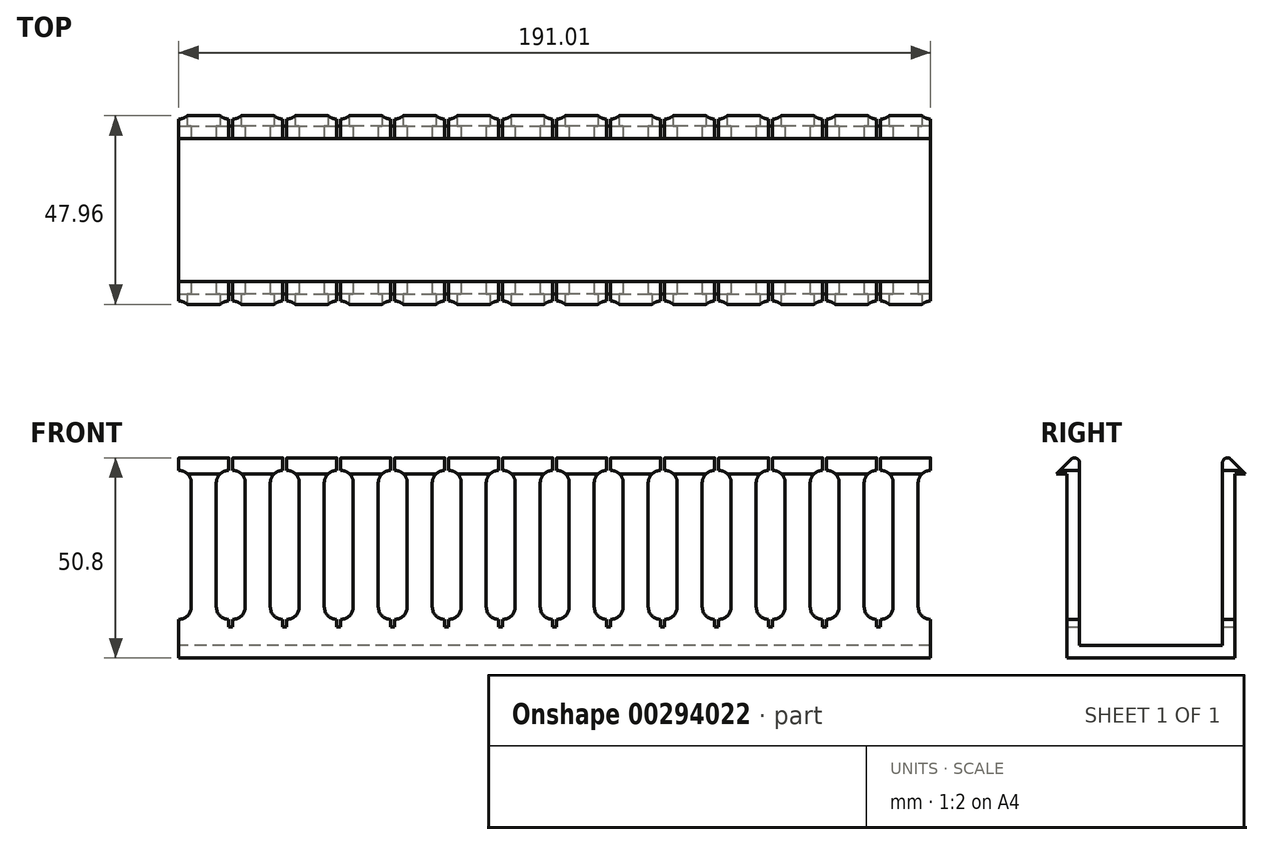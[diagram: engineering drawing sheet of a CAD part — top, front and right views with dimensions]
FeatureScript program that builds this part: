
annotation { "Feature Type Name" : "Feature", "Feature Type Description" : "" }
export const myFeature = defineFeature(function(context is Context, id is Id, definition is map)
    precondition{}
    {
        {
            var Q0;
            Q0=qCreatedBy(makeId("Right.planeOp"),FACE);
            var sketch = newSketch(context, id + "F0", { "sketchPlane" : qUnion([Q0])});
            skLineSegment(sketch, "E0", {"start": v(18.16, 7.87) * mm, "end": v(18.16, 49.53) * mm});
            skArc(sketch, "E1", {"start": v(20.33, 50.43) * mm, "mid": v(18.94, 50.7) * mm, "end": v(18.16, 49.53) * mm});
            skLineSegment(sketch, "E2", {"start": v(20.33, 50.43) * mm, "end": v(23.98, 46.78) * mm});
            skLineSegment(sketch, "E3", {"start": v(23.98, 46.78) * mm, "end": v(21.34, 46.78) * mm});
            skLineSegment(sketch, "E4", {"start": v(21.34, 46.78) * mm, "end": v(21.34, 7.87) * mm});
            skLineSegment(sketch, "E5", {"start": v(21.34, 7.87) * mm, "end": v(18.16, 7.87) * mm});
            skLineSegment(sketch, "E6", {"start": v(18.16, 7.87) * mm, "end": v(18.16, 3.18) * mm});
            skLineSegment(sketch, "E7", {"start": v(18.16, 3.18) * mm, "end": v(0, 3.17) * mm});
            skLineSegment(sketch, "E8", {"start": v(21.34, 7.87) * mm, "end": v(21.34, 0) * mm});
            skLineSegment(sketch, "E9", {"start": v(21.34, 0) * mm, "end": v(0, 0) * mm});
            skLineSegment(sketch, "E10", {"start": v(0, 14.6) * mm, "end": v(0, -14.6) * mm, "construction": true});
            skLineSegment(sketch, "E11.MirrorCS", {"start": v(-18.16, 3.18) * mm, "end": v(0, 3.17) * mm});
            skLineSegment(sketch, "E12.MirrorCS", {"start": v(-21.34, 0) * mm, "end": v(0, 0) * mm});
            skLineSegment(sketch, "E13.MirrorCS", {"start": v(-18.16, 7.87) * mm, "end": v(-18.16, 3.18) * mm});
            skLineSegment(sketch, "E14.MirrorCS", {"start": v(-21.34, 7.87) * mm, "end": v(-21.34, 0) * mm});
            skLineSegment(sketch, "E15.MirrorCS", {"start": v(-18.16, 7.87) * mm, "end": v(-18.16, 49.53) * mm});
            skLineSegment(sketch, "E16.MirrorCS", {"start": v(-21.34, 46.78) * mm, "end": v(-21.34, 7.87) * mm});
            skLineSegment(sketch, "E17.MirrorCS", {"start": v(-23.98, 46.78) * mm, "end": v(-21.34, 46.78) * mm});
            skLineSegment(sketch, "E18.MirrorCS", {"start": v(-20.33, 50.43) * mm, "end": v(-23.98, 46.78) * mm});
            skArc(sketch, "E19.MirrorCS", {"start": v(-20.33, 50.43) * mm, "mid": v(-18.94, 50.7) * mm, "end": v(-18.16, 49.53) * mm});
            skLineSegment(sketch, "E20", {"start": v(-18.16, 7.87) * mm, "end": v(-21.34, 7.87) * mm});
            skSolve(sketch);
        }
        {
            var Q0;
            Q0 = qSketchRegion(id + "F0", true);
            extrude(context, id + "F1", {"entities" : qUnion([Q0]), "endBound" : BoundingType.SYMMETRIC, "depth" : 12.7 * mm});
        }
        {
            var Q0;
            Q0=qCreatedBy(makeId("Front.planeOp"),FACE);
            var sketch = newSketch(context, id + "F2", { "sketchPlane" : qUnion([Q0])});
            skArc(sketch, "E21", {"start": v(-3.18, 44.45) * mm, "mid": v(-6.35, 47.62) * mm, "end": v(-9.53, 44.45) * mm});
            skLineSegment(sketch, "E22", {"start": v(0, 50.8) * mm, "end": v(0, 0) * mm, "construction": true});
            skPoint(sketch, "E23.startSnap0", {"position": v(0, 25.4) * mm});
            skArc(sketch, "E24", {"start": v(-9.53, 12.95) * mm, "mid": v(-6.35, 9.78) * mm, "end": v(-3.18, 12.95) * mm});
            skArc(sketch, "E25.MirrorC", {"start": v(3.18, 44.45) * mm, "mid": v(6.35, 47.62) * mm, "end": v(9.53, 44.45) * mm});
            skArc(sketch, "E26.MirrorC", {"start": v(9.53, 12.95) * mm, "mid": v(6.35, 9.78) * mm, "end": v(3.18, 12.95) * mm});
            skLineSegment(sketch, "E27", {"start": v(-3.18, 44.45) * mm, "end": v(-3.18, 12.95) * mm});
            skLineSegment(sketch, "E28", {"start": v(-9.53, 44.45) * mm, "end": v(-9.52, 12.95) * mm});
            skLineSegment(sketch, "E29.MirrorCS", {"start": v(9.53, 44.45) * mm, "end": v(9.52, 12.95) * mm});
            skLineSegment(sketch, "E30.MirrorCS", {"start": v(3.18, 44.45) * mm, "end": v(3.18, 12.95) * mm});
            skLineSegment(sketch, "E31", {"start": v(-6.86, 50.8) * mm, "end": v(-6.86, 0) * mm, "construction": true});
            skLineSegment(sketch, "E32", {"start": v(-6.86, 7.87) * mm, "end": v(-6.35, 7.87) * mm});
            skLineSegment(sketch, "E33", {"start": v(-6.86, 7.87) * mm, "end": v(-6.86, 0) * mm});
            skLineSegment(sketch, "E34", {"start": v(-6.35, 0) * mm, "end": v(-6.35, 7.87) * mm});
            skLineSegment(sketch, "E35", {"start": v(-6.86, 0) * mm, "end": v(-6.35, 0) * mm});
            skLineSegment(sketch, "E36.MirrorCS", {"start": v(6.35, 0) * mm, "end": v(6.35, 7.87) * mm});
            skLineSegment(sketch, "E37.MirrorCS", {"start": v(6.86, 7.87) * mm, "end": v(6.35, 7.87) * mm});
            skLineSegment(sketch, "E38.MirrorCS", {"start": v(6.86, 0) * mm, "end": v(6.35, 0) * mm});
            skLineSegment(sketch, "E39", {"start": v(6.86, 7.87) * mm, "end": v(6.86, 0) * mm});
            skSolve(sketch);
        }
        {
            var Q0;
            Q0 = qSketchRegion(id + "F2", true);
            extrude(context, id + "F3", {"entities" : qUnion([Q0]), "operationType" : NewBodyOperationType.REMOVE, "endBound" : BoundingType.SYMMETRIC, "oppositeDirection" : true, "depth" : 50.8 * mm});
        }
        {
            var Q0;
            Q0=makeQuery(id+"F2.imprint","IMPRINT",FACE,{"disambiguationData":[TD([[makeQuery(id+"F2.imprint","IMPRINT",EDGE,{"derivedFrom":sQuery(id+"F2.wireOp",EDGE,"E32")}),-1.0]])]});
            var Q1;
            Q1=makeQuery(id+"F2.imprint","IMPRINT",FACE,{"disambiguationData":[TD([[makeQuery(id+"F2.imprint","IMPRINT",EDGE,{"derivedFrom":sQuery(id+"F2.wireOp",EDGE,"E36.MirrorCS")}),-1.0]])]});
            extrude(context, id + "F4", {"entities" : qUnion([Q0, Q1]), "operationType" : NewBodyOperationType.ADD, "endBound" : BoundingType.SYMMETRIC, "depth" : 42.67 * mm});
        }
        {
            var Q0;
            Q0=qCreatedBy(makeId("Right.planeOp"),FACE);
            var sketch = newSketch(context, id + "F5", { "sketchPlane" : qUnion([Q0])});
            skLineSegment(sketch, "E40.bottom", {"start": v(-18.16, 7.87) * mm, "end": v(18.16, 7.87) * mm});
            skLineSegment(sketch, "E40.top", {"start": v(-18.16, 3.18) * mm, "end": v(18.16, 3.18) * mm});
            skLineSegment(sketch, "E40.left", {"start": v(-18.16, 7.87) * mm, "end": v(-18.16, 3.18) * mm});
            skLineSegment(sketch, "E40.right", {"start": v(18.16, 7.87) * mm, "end": v(18.16, 3.18) * mm});
            skSolve(sketch);
        }
        {
            var Q0;
            Q0 = qSketchRegion(id + "F5", true);
            extrude(context, id + "F6", {"entities" : qUnion([Q0]), "operationType" : NewBodyOperationType.REMOVE, "endBound" : BoundingType.SYMMETRIC, "depth" : 25.4 * mm});
        }
        {
            var Q0;
            Q0=makeQuery(id+"F1.opExtrude","SWEPT_BODY",BODY,{"disambiguationData":[OSD([sQuery(id+"F0.wireOp",EDGE,"E0"),sQuery(id+"F0.wireOp",EDGE,"E1"),sQuery(id+"F0.wireOp",EDGE,"E2"),sQuery(id+"F0.wireOp",EDGE,"E3"),sQuery(id+"F0.wireOp",EDGE,"E4"),sQuery(id+"F0.wireOp",EDGE,"E6"),sQuery(id+"F0.wireOp",EDGE,"E7"),sQuery(id+"F0.wireOp",EDGE,"E8"),sQuery(id+"F0.wireOp",EDGE,"E9"),sQuery(id+"F0.wireOp",EDGE,"E11.MirrorCS"),sQuery(id+"F0.wireOp",EDGE,"E12.MirrorCS"),sQuery(id+"F0.wireOp",EDGE,"E13.MirrorCS"),sQuery(id+"F0.wireOp",EDGE,"E14.MirrorCS"),sQuery(id+"F0.wireOp",EDGE,"E15.MirrorCS"),sQuery(id+"F0.wireOp",EDGE,"E16.MirrorCS"),sQuery(id+"F0.wireOp",EDGE,"E17.MirrorCS"),sQuery(id+"F0.wireOp",EDGE,"E18.MirrorCS"),sQuery(id+"F0.wireOp",EDGE,"E19.MirrorCS")])]});
            var Q1;
            Q1=makeQuery(id+"F4.opExtrude","SWEPT_FACE",FACE,{"disambiguationData":[OSD([sQuery(id+"F2.wireOp",EDGE,"E33")])]});
            mirror(context, id + "F7", {"operationType" : NewBodyOperationType.ADD, "entities" : qUnion([Q0]), "mirrorPlane" : qUnion([Q1])});
        }
        {
            var Q0;
            Q0=makeQuery(id+"F1.opExtrude","SWEPT_BODY",BODY,{"disambiguationData":[OSD([sQuery(id+"F0.wireOp",EDGE,"E0"),sQuery(id+"F0.wireOp",EDGE,"E1"),sQuery(id+"F0.wireOp",EDGE,"E2"),sQuery(id+"F0.wireOp",EDGE,"E3"),sQuery(id+"F0.wireOp",EDGE,"E4"),sQuery(id+"F0.wireOp",EDGE,"E6"),sQuery(id+"F0.wireOp",EDGE,"E7"),sQuery(id+"F0.wireOp",EDGE,"E8"),sQuery(id+"F0.wireOp",EDGE,"E9"),sQuery(id+"F0.wireOp",EDGE,"E11.MirrorCS"),sQuery(id+"F0.wireOp",EDGE,"E12.MirrorCS"),sQuery(id+"F0.wireOp",EDGE,"E13.MirrorCS"),sQuery(id+"F0.wireOp",EDGE,"E14.MirrorCS"),sQuery(id+"F0.wireOp",EDGE,"E15.MirrorCS"),sQuery(id+"F0.wireOp",EDGE,"E16.MirrorCS"),sQuery(id+"F0.wireOp",EDGE,"E17.MirrorCS"),sQuery(id+"F0.wireOp",EDGE,"E18.MirrorCS"),sQuery(id+"F0.wireOp",EDGE,"E19.MirrorCS")])]});
            var Q1;
            Q1=makeQuery(id+"F7.opPattern","COPY",FACE,{"derivedFrom":makeQuery(id+"F4.opExtrude","SWEPT_FACE",FACE,{"disambiguationData":[OSD([sQuery(id+"F2.wireOp",EDGE,"E39")])]}),"instanceName":"1"});
            mirror(context, id + "F8", {"operationType" : NewBodyOperationType.ADD, "entities" : qUnion([Q0]), "mirrorPlane" : qUnion([Q1])});
        }
        {
            var Q0;
            Q0=makeQuery(id+"F1.opExtrude","SWEPT_BODY",BODY,{"disambiguationData":[OSD([sQuery(id+"F0.wireOp",EDGE,"E0"),sQuery(id+"F0.wireOp",EDGE,"E1"),sQuery(id+"F0.wireOp",EDGE,"E2"),sQuery(id+"F0.wireOp",EDGE,"E3"),sQuery(id+"F0.wireOp",EDGE,"E4"),sQuery(id+"F0.wireOp",EDGE,"E6"),sQuery(id+"F0.wireOp",EDGE,"E7"),sQuery(id+"F0.wireOp",EDGE,"E8"),sQuery(id+"F0.wireOp",EDGE,"E9"),sQuery(id+"F0.wireOp",EDGE,"E11.MirrorCS"),sQuery(id+"F0.wireOp",EDGE,"E12.MirrorCS"),sQuery(id+"F0.wireOp",EDGE,"E13.MirrorCS"),sQuery(id+"F0.wireOp",EDGE,"E14.MirrorCS"),sQuery(id+"F0.wireOp",EDGE,"E15.MirrorCS"),sQuery(id+"F0.wireOp",EDGE,"E16.MirrorCS"),sQuery(id+"F0.wireOp",EDGE,"E17.MirrorCS"),sQuery(id+"F0.wireOp",EDGE,"E18.MirrorCS"),sQuery(id+"F0.wireOp",EDGE,"E19.MirrorCS")])]});
            var Q1;
            Q1=makeQuery(id+"F8.opPattern","COPY",FACE,{"derivedFrom":makeQuery(id+"F4.opExtrude","SWEPT_FACE",FACE,{"disambiguationData":[OSD([sQuery(id+"F2.wireOp",EDGE,"E39")])]}),"instanceName":"1"});
            mirror(context, id + "F9", {"operationType" : NewBodyOperationType.ADD, "entities" : qUnion([Q0]), "mirrorPlane" : qUnion([Q1])});
        }
        {
            var Q0;
            Q0=makeQuery(id+"F1.opExtrude","SWEPT_BODY",BODY,{"disambiguationData":[OSD([sQuery(id+"F0.wireOp",EDGE,"E0"),sQuery(id+"F0.wireOp",EDGE,"E1"),sQuery(id+"F0.wireOp",EDGE,"E2"),sQuery(id+"F0.wireOp",EDGE,"E3"),sQuery(id+"F0.wireOp",EDGE,"E4"),sQuery(id+"F0.wireOp",EDGE,"E6"),sQuery(id+"F0.wireOp",EDGE,"E7"),sQuery(id+"F0.wireOp",EDGE,"E8"),sQuery(id+"F0.wireOp",EDGE,"E9"),sQuery(id+"F0.wireOp",EDGE,"E11.MirrorCS"),sQuery(id+"F0.wireOp",EDGE,"E12.MirrorCS"),sQuery(id+"F0.wireOp",EDGE,"E13.MirrorCS"),sQuery(id+"F0.wireOp",EDGE,"E14.MirrorCS"),sQuery(id+"F0.wireOp",EDGE,"E15.MirrorCS"),sQuery(id+"F0.wireOp",EDGE,"E16.MirrorCS"),sQuery(id+"F0.wireOp",EDGE,"E17.MirrorCS"),sQuery(id+"F0.wireOp",EDGE,"E18.MirrorCS"),sQuery(id+"F0.wireOp",EDGE,"E19.MirrorCS")])]});
            var Q1;
            Q1=makeQuery(id+"F9.opPattern","COPY",FACE,{"derivedFrom":makeQuery(id+"F4.opExtrude","SWEPT_FACE",FACE,{"disambiguationData":[OSD([sQuery(id+"F2.wireOp",EDGE,"E39")])]}),"instanceName":"1"});
            mirror(context, id + "F10", {"operationType" : NewBodyOperationType.ADD, "entities" : qUnion([Q0]), "mirrorPlane" : qUnion([Q1])});
        }
        {
            var Q0;
            Q0=qCreatedBy(makeId("Front.planeOp"),FACE);
            var sketch = newSketch(context, id + "F11", { "sketchPlane" : qUnion([Q0])});
            skLineSegment(sketch, "E41.bottom", {"start": v(6.35, 7.87) * mm, "end": v(6.86, 7.87) * mm});
            skLineSegment(sketch, "E41.top", {"start": v(6.35, 0) * mm, "end": v(6.86, 0) * mm});
            skLineSegment(sketch, "E41.left", {"start": v(6.35, 7.87) * mm, "end": v(6.35, 0) * mm});
            skLineSegment(sketch, "E41.right", {"start": v(6.86, 7.87) * mm, "end": v(6.86, 0) * mm});
            skLineSegment(sketch, "E42.bottom", {"start": v(-212.6, 7.87) * mm, "end": v(-212.09, 7.87) * mm});
            skLineSegment(sketch, "E42.top", {"start": v(-212.6, 0) * mm, "end": v(-212.09, 0) * mm});
            skLineSegment(sketch, "E42.left", {"start": v(-212.6, 7.87) * mm, "end": v(-212.6, 0) * mm});
            skLineSegment(sketch, "E42.right", {"start": v(-212.09, 7.87) * mm, "end": v(-212.09, 0) * mm});
            skSolve(sketch);
        }
        {
            var Q0;
            Q0 = qSketchRegion(id + "F11", true);
            extrude(context, id + "F12", {"entities" : qUnion([Q0]), "operationType" : NewBodyOperationType.REMOVE, "endBound" : BoundingType.SYMMETRIC, "oppositeDirection" : true, "depth" : 50.8 * mm});
        }
        {
            var Q0;
            Q0=qCreatedBy(makeId("Front.planeOp"),FACE);
            var sketch = newSketch(context, id + "F13", { "sketchPlane" : qUnion([Q0])});
            skLineSegment(sketch, "E43.bottom", {"start": v(-212.09, 0) * mm, "end": v(-184.66, 0) * mm});
            skLineSegment(sketch, "E43.top", {"start": v(-212.09, 50.8) * mm, "end": v(-184.66, 50.8) * mm});
            skLineSegment(sketch, "E43.left", {"start": v(-212.09, 0) * mm, "end": v(-212.09, 50.8) * mm});
            skLineSegment(sketch, "E43.right", {"start": v(-184.66, 0) * mm, "end": v(-184.66, 50.8) * mm});
            skSolve(sketch);
        }
        {
            var Q0;
            Q0 = qSketchRegion(id + "F13", true);
            extrude(context, id + "F14", {"entities" : qUnion([Q0]), "operationType" : NewBodyOperationType.REMOVE, "endBound" : BoundingType.SYMMETRIC, "oppositeDirection" : true, "depth" : 50.8 * mm});
        }
    });
